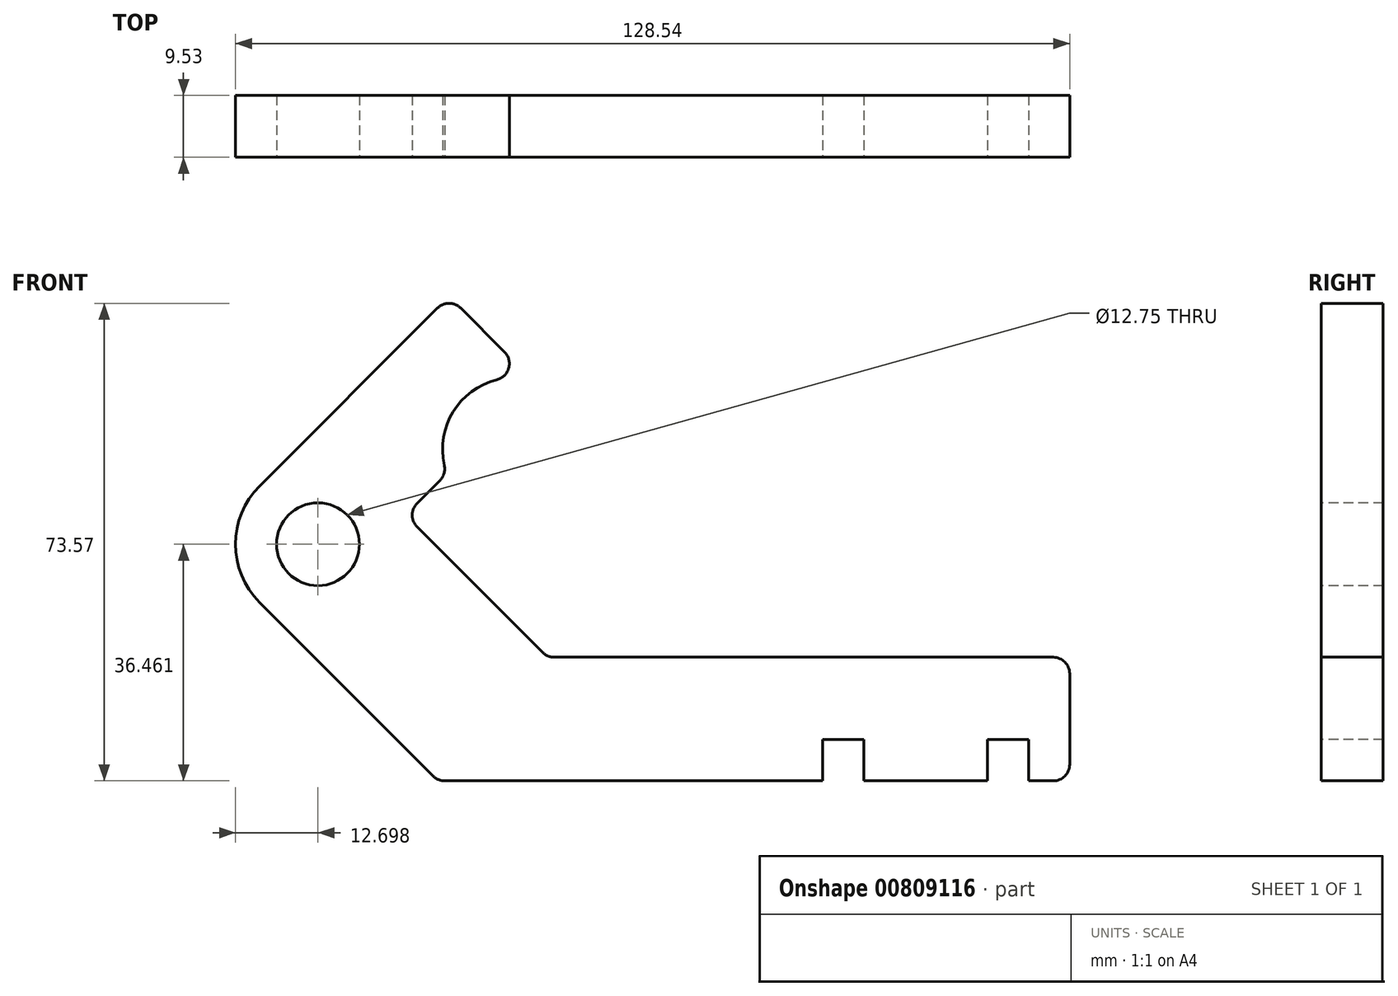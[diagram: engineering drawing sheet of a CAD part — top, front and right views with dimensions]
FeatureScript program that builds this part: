
annotation { "Feature Type Name" : "Feature", "Feature Type Description" : "" }
export const myFeature = defineFeature(function(context is Context, id is Id, definition is map)
    precondition{}
    {
        {
            var Q0;
            Q0=qCreatedBy(makeId("Front.planeOp"),FACE);
            var sketch = newSketch(context, id + "F0", { "sketchPlane" : qUnion([Q0])});
            skArc(sketch, "E0", {"start": v(33.41, 24.39) * mm, "mid": v(22.5, 21.07) * mm, "end": v(20.26, 9.87) * mm});
            skLineSegment(sketch, "E1", {"start": v(30.73, 13.6) * mm, "end": v(4.61, 13.6) * mm, "construction": true});
            skLineSegment(sketch, "E2", {"start": v(30.73, 13.6) * mm, "end": v(13.89, 30.44) * mm, "construction": true});
            skLineSegment(sketch, "E3.0", {"start": v(33.41, 24.39) * mm, "end": v(20.62, 37.18) * mm});
            skLineSegment(sketch, "E4", {"start": v(22.87, 21.46) * mm, "end": v(-8.56, -9.97) * mm, "construction": true});
            skLineSegment(sketch, "E5.0", {"start": v(4.93, -5.5) * mm, "end": v(-4.28, 3.71) * mm, "construction": true});
            skCircle(sketch, "E6", {"center": v(0.42, -0.99) * mm, "radius": 6.38 * mm});
            skLineSegment(sketch, "E7.0", {"start": v(20.62, 37.18) * mm, "end": v(-8.56, 8) * mm});
            skLineSegment(sketch, "E8.0", {"start": v(35.8, -18.4) * mm, "end": v(13.89, 3.5) * mm});
            skLineSegment(sketch, "E9.0", {"start": v(18.92, -37.45) * mm, "end": v(-8.56, -9.97) * mm});
            skLineSegment(sketch, "E10.0", {"start": v(20.26, 9.87) * mm, "end": v(13.89, 3.5) * mm});
            skLineSegment(sketch, "E11", {"start": v(9.4, -27.93) * mm, "end": v(116.26, -27.93) * mm, "construction": true});
            skLineSegment(sketch, "E12.0", {"start": v(26.27, -8.88) * mm, "end": v(116.26, -8.88) * mm, "construction": true});
            skLineSegment(sketch, "E13.0", {"start": v(52.76, -27.93) * mm, "end": v(52.76, -8.88) * mm, "construction": true});
            skArc(sketch, "E14.trimOffspring", {"start": v(-8.56, 8) * mm, "mid": v(-12.28, -0.99) * mm, "end": v(-8.56, -9.97) * mm});
            skLineSegment(sketch, "E15.0", {"start": v(116.26, -37.45) * mm, "end": v(116.26, -18.4) * mm});
            skLineSegment(sketch, "E16.bottom", {"start": v(109.9, -8.88) * mm, "end": v(103.56, -8.88) * mm, "construction": true});
            skLineSegment(sketch, "E16.top", {"start": v(109.9, -15.23) * mm, "end": v(103.56, -15.23) * mm, "construction": true});
            skLineSegment(sketch, "E16.left", {"start": v(109.9, -31.1) * mm, "end": v(109.9, -37.45) * mm});
            skLineSegment(sketch, "E16.right", {"start": v(103.56, -31.1) * mm, "end": v(103.56, -37.45) * mm});
            skLineSegment(sketch, "E17.bottom", {"start": v(78.16, -8.88) * mm, "end": v(84.5, -8.88) * mm, "construction": true});
            skLineSegment(sketch, "E17.top", {"start": v(78.16, -15.23) * mm, "end": v(84.5, -15.23) * mm, "construction": true});
            skLineSegment(sketch, "E17.left", {"start": v(78.16, -31.1) * mm, "end": v(78.16, -37.45) * mm});
            skLineSegment(sketch, "E17.right", {"start": v(84.5, -31.1) * mm, "end": v(84.5, -37.45) * mm});
            skLineSegment(sketch, "E18.0", {"start": v(78.16, -31.1) * mm, "end": v(84.5, -31.1) * mm});
            skLineSegment(sketch, "E19.0", {"start": v(18.92, -37.45) * mm, "end": v(116.26, -37.45) * mm});
            skLineSegment(sketch, "E20.0", {"start": v(35.8, -18.4) * mm, "end": v(116.26, -18.4) * mm});
            skLineSegment(sketch, "E21", {"start": v(103.56, -31.1) * mm, "end": v(109.9, -31.1) * mm});
            skLineSegment(sketch, "E22", {"start": v(116.26, -18.4) * mm, "end": v(116.26, -8.88) * mm, "construction": true});
            skSolve(sketch);
        }
        {
            var Q0;
            Q0=makeQuery(id+"F0.imprint","IMPRINT",FACE,{"disambiguationData":[TD([[makeQuery(id+"F0.imprint","IMPRINT",EDGE,{"derivedFrom":sQuery(id+"F0.wireOp",EDGE,"E0")}),-1.0]])]});
            extrude(context, id + "F1", {"entities" : qUnion([Q0]), "oppositeDirection" : true, "depth" : 9.52 * mm, "offsetDistance" : 25.4 * mm});
        }
        {
            var Q0;
            Q0=makeQuery(id+"F1.opExtrude","SWEPT_EDGE",EDGE,{"disambiguationData":[OSD([sQuery(id+"F0.wireOp",EDGE,"E0"),sQuery(id+"F0.wireOp",EDGE,"E3.0")])]});
            var Q1;
            Q1=makeQuery(id+"F1.opExtrude","SWEPT_EDGE",EDGE,{"disambiguationData":[OSD([sQuery(id+"F0.wireOp",EDGE,"E0"),sQuery(id+"F0.wireOp",EDGE,"E10.0")])]});
            fillet(context, id + "F2", {"entities" : qUnion([Q0, Q1]), "radius" : 2.54 * mm, "tangentPropagation" : true, "allowEdgeOverflow" : false});
        }
        {
            var Q0;
            Q0=makeQuery(id+"F1.opExtrude","SWEPT_EDGE",EDGE,{"disambiguationData":[OSD([sQuery(id+"F0.wireOp",EDGE,"E8.0"),sQuery(id+"F0.wireOp",EDGE,"E10.0")])]});
            var Q1;
            Q1=makeQuery(id+"F1.opExtrude","SWEPT_EDGE",EDGE,{"disambiguationData":[OSD([sQuery(id+"F0.wireOp",EDGE,"E8.0"),sQuery(id+"F0.wireOp",EDGE,"E20.0")])]});
            var Q2;
            Q2=makeQuery(id+"F1.opExtrude","SWEPT_EDGE",EDGE,{"disambiguationData":[OSD([sQuery(id+"F0.wireOp",EDGE,"E9.0"),sQuery(id+"F0.wireOp",EDGE,"E19.0")])]});
            var Q3;
            Q3=makeQuery(id+"F1.opExtrude","SWEPT_EDGE",EDGE,{"disambiguationData":[OSD([sQuery(id+"F0.wireOp",EDGE,"E15.0"),sQuery(id+"F0.wireOp",EDGE,"E20.0")])]});
            var Q4;
            Q4=makeQuery(id+"F1.opExtrude","SWEPT_EDGE",EDGE,{"disambiguationData":[OSD([sQuery(id+"F0.wireOp",EDGE,"E15.0"),sQuery(id+"F0.wireOp",EDGE,"E19.0")])]});
            var Q5;
            Q5=makeQuery(id+"F1.opExtrude","SWEPT_EDGE",EDGE,{"disambiguationData":[OSD([sQuery(id+"F0.wireOp",EDGE,"E3.0"),sQuery(id+"F0.wireOp",EDGE,"E7.0")])]});
            fillet(context, id + "F3", {"entities" : qUnion([Q0, Q1, Q2, Q3, Q4, Q5]), "radius" : 2.54 * mm, "tangentPropagation" : true, "allowEdgeOverflow" : false});
        }
    });
